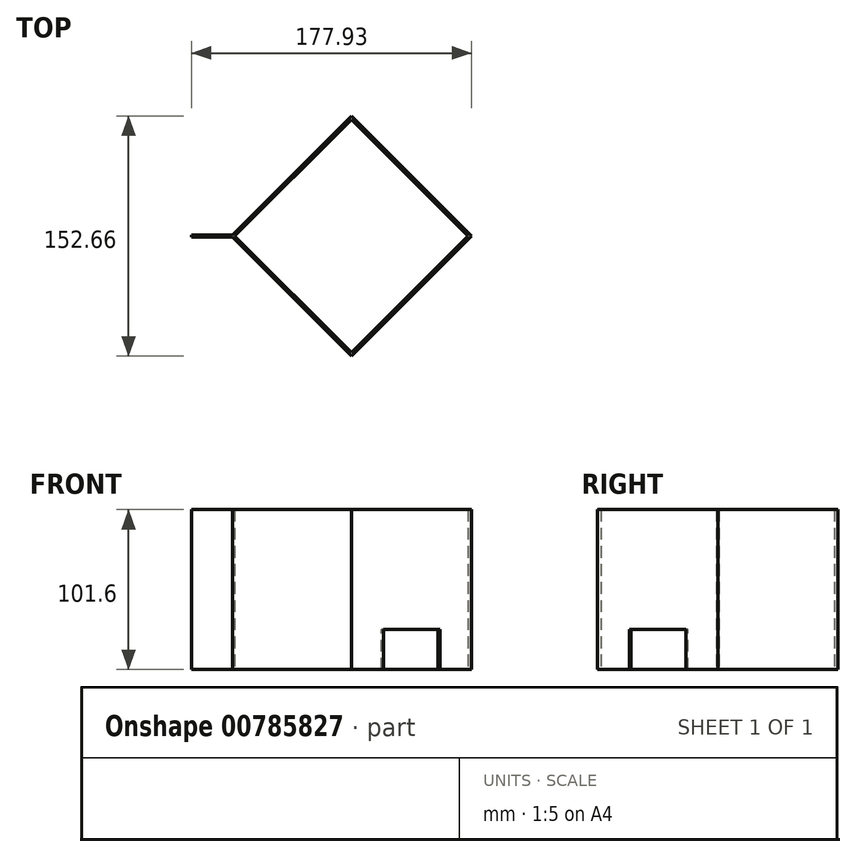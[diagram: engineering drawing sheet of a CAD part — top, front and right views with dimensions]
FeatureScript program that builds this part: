
annotation { "Feature Type Name" : "Feature", "Feature Type Description" : "" }
export const myFeature = defineFeature(function(context is Context, id is Id, definition is map)
    precondition{}
    {
        {
            var Q0;
            Q0=qCreatedBy(makeId("Top.planeOp"),FACE);
            var sketch = newSketch(context, id + "F0", { "sketchPlane" : qUnion([Q0])});
            skLineSegment(sketch, "E0.bottom", {"start": v(101.6, 101.6) * mm, "end": v(-101.6, 101.6) * mm});
            skLineSegment(sketch, "E0.top", {"start": v(101.6, -101.6) * mm, "end": v(-101.6, -101.6) * mm});
            skLineSegment(sketch, "E0.left", {"start": v(101.6, 101.6) * mm, "end": v(101.6, -101.6) * mm});
            skLineSegment(sketch, "E0.right", {"start": v(-101.6, 101.6) * mm, "end": v(-101.6, -101.6) * mm});
            skPoint(sketch, "E0.middle", {"position": v(0, 0) * mm});
            skLineSegment(sketch, "E1.bottom", {"start": v(0, -76.33) * mm, "end": v(-76.33, 0) * mm});
            skLineSegment(sketch, "E1.top", {"start": v(76.33, 0) * mm, "end": v(0, 76.33) * mm});
            skLineSegment(sketch, "E1.left", {"start": v(0, -76.33) * mm, "end": v(76.33, 0) * mm});
            skLineSegment(sketch, "E1.right", {"start": v(-76.33, 0) * mm, "end": v(0, 76.33) * mm});
            skLineSegment(sketch, "E2", {"start": v(0, -101.6) * mm, "end": v(0, -101.6) * mm});
            skLineSegment(sketch, "E3", {"start": v(0, 101.6) * mm, "end": v(0, 0) * mm});
            skSolve(sketch);
        }
        {
            var Q0;
            Q0=makeQuery(id+"F0.imprint","IMPRINT",FACE,{"disambiguationData":[TD([[makeQuery(id+"F0.imprint","IMPRINT",EDGE,{"derivedFrom":sQuery(id+"F0.wireOp",EDGE,"E1.bottom")}),-1.0]])]});
            extrude(context, id + "F1", {"entities" : qUnion([Q0]), "depth" : 101.6 * mm, "offsetDistance" : 25.4 * mm});
        }
        {
            var Q0;
            Q0=makeQuery(id+"F1.opExtrude","CAP_FACE",FACE,{"disambiguationData":[OSD([sQuery(id+"F0.wireOp",EDGE,"E1.bottom"),sQuery(id+"F0.wireOp",EDGE,"E1.top"),sQuery(id+"F0.wireOp",EDGE,"E1.left"),sQuery(id+"F0.wireOp",EDGE,"E1.right")])],"isStart":false});
            var Q1;
            Q1=makeQuery(id+"F1.opExtrude","CAP_FACE",FACE,{"disambiguationData":[OSD([sQuery(id+"F0.wireOp",EDGE,"E1.bottom"),sQuery(id+"F0.wireOp",EDGE,"E1.top"),sQuery(id+"F0.wireOp",EDGE,"E1.left"),sQuery(id+"F0.wireOp",EDGE,"E1.right")])],"isStart":true});
            shell(context, id + "F2", {"entities" : qUnion([Q0, Q1]), "thickness" : 1.57 * mm});
        }
        {
            var Q0;
            Q0=makeQuery(id+"F1.opExtrude","CAP_FACE",FACE,{"disambiguationData":[OSD([sQuery(id+"F0.wireOp",EDGE,"E1.bottom"),sQuery(id+"F0.wireOp",EDGE,"E1.top"),sQuery(id+"F0.wireOp",EDGE,"E1.left"),sQuery(id+"F0.wireOp",EDGE,"E1.right")])],"isStart":false});
            var sketch = newSketch(context, id + "F3", { "sketchPlane" : qUnion([Q0])});
            skLineSegment(sketch, "E4.bottom", {"start": v(-73.32, -0.79) * mm, "end": v(-101.6, -0.79) * mm});
            skLineSegment(sketch, "E4.top", {"start": v(-73.32, 0.79) * mm, "end": v(-101.6, 0.79) * mm});
            skLineSegment(sketch, "E4.left", {"start": v(-73.32, -0.79) * mm, "end": v(-73.32, 0.79) * mm});
            skLineSegment(sketch, "E4.right", {"start": v(-101.6, -0.79) * mm, "end": v(-101.6, 0.79) * mm});
            skPoint(sketch, "E4.middle", {"position": v(-87.46, 0) * mm});
            skLineSegment(sketch, "E5.0", {"start": v(-74.1, 0) * mm, "end": v(0, 74.1) * mm});
            skLineSegment(sketch, "E6.0.0", {"start": v(74.1, 0) * mm, "end": v(0, -74.1) * mm});
            skLineSegment(sketch, "E6.0.1", {"start": v(0, 74.1) * mm, "end": v(74.1, 0) * mm});
            skLineSegment(sketch, "E6.0.3", {"start": v(0, -74.1) * mm, "end": v(-74.1, 0) * mm});
            skSolve(sketch);
        }
        {
            var Q0;
            {var subQ5=sQuery(id+"F3.wireOp",EDGE,"E4.right");Q0=makeQuery(id+"F3.imprint","IMPRINT",FACE,{"disambiguationData":[TD([[makeQuery(id+"F3.imprint","IMPRINT",EDGE,{"derivedFrom":subQ5}),-1.0]])]});}
            var Q1;
            {var subQ6=makeQuery(id+"F1.opExtrude","CAP_EDGE",EDGE,{"disambiguationData":[OSD([sQuery(id+"F0.wireOp",EDGE,"E1.bottom")])],"isStart":false});var subQ10=makeQuery(id+"F1.opExtrude","CAP_EDGE",EDGE,{"disambiguationData":[OSD([sQuery(id+"F0.wireOp",EDGE,"E1.right")])],"isStart":false});var subQ12=makeQuery(id+"F3.imprint","INTERSECT",VERTEX,{"derivedFrom":[subQ6,subQ10]});Q1=makeQuery(id+"F3.imprint","IMPRINT",FACE,{"disambiguationData":[TD([[makeQuery(id+"F3.imprint","IMPRINT",EDGE,{"disambiguationData":[TD([[subQ12,1.0]])],"derivedFrom":subQ6}),-1.0]])]});}
            var Q2;
            Q2=makeQuery(id+"F1.opExtrude","CAP_FACE",FACE,{"disambiguationData":[OSD([sQuery(id+"F0.wireOp",EDGE,"E1.bottom"),sQuery(id+"F0.wireOp",EDGE,"E1.top"),sQuery(id+"F0.wireOp",EDGE,"E1.left"),sQuery(id+"F0.wireOp",EDGE,"E1.right")])],"isStart":true});
            extrude(context, id + "F4", {"entities" : qUnion([Q0, Q1]), "operationType" : NewBodyOperationType.ADD, "endBound" : BoundingType.UP_TO_SURFACE, "oppositeDirection" : true, "depth" : 25.4 * mm, "endBoundEntityFace" : qUnion([Q2]), "offsetDistance" : 25.4 * mm});
        }
        {
            var Q0;
            Q0=qCreatedBy(makeId("Top.planeOp"),FACE);
            var sketch = newSketch(context, id + "F5", { "sketchPlane" : qUnion([Q0])});
            skCircle(sketch, "E7", {"center": v(0, 0) * mm, "radius": 11.35 * mm});
            skSolve(sketch);
        }
        {
            var Q0;
            Q0=makeQuery(id+"F1.opExtrude","SWEPT_FACE",FACE,{"disambiguationData":[OSD([sQuery(id+"F0.wireOp",EDGE,"E1.left")])]});
            var sketch = newSketch(context, id + "F6", { "sketchPlane" : qUnion([Q0])});
            skLineSegment(sketch, "E8.bottom", {"start": v(25.4, 0) * mm, "end": v(-25.4, 0) * mm});
            skLineSegment(sketch, "E8.top", {"start": v(25.4, 25.4) * mm, "end": v(-25.4, 25.4) * mm});
            skLineSegment(sketch, "E8.left", {"start": v(25.4, 0) * mm, "end": v(25.4, 25.4) * mm});
            skLineSegment(sketch, "E8.right", {"start": v(-25.4, 0) * mm, "end": v(-25.4, 25.4) * mm});
            skPoint(sketch, "E8.middle", {"position": v(0, 12.7) * mm});
            skSolve(sketch);
        }
        {
            var Q0;
            Q0 = qSketchRegion(id + "F6", true);
            extrude(context, id + "F7", {"entities" : qUnion([Q0]), "operationType" : NewBodyOperationType.REMOVE, "endBound" : BoundingType.UP_TO_NEXT, "oppositeDirection" : true, "depth" : 25.4 * mm, "offsetDistance" : 25.4 * mm});
        }
        {
            var Q0;
            Q0=qCreatedBy(makeId("Top.planeOp"),FACE);
            var sketch = newSketch(context, id + "F8", { "sketchPlane" : qUnion([Q0])});
            skCircle(sketch, "E9", {"center": v(0, 0) * mm, "radius": 20.4 * mm});
            skSolve(sketch);
        }
    });
